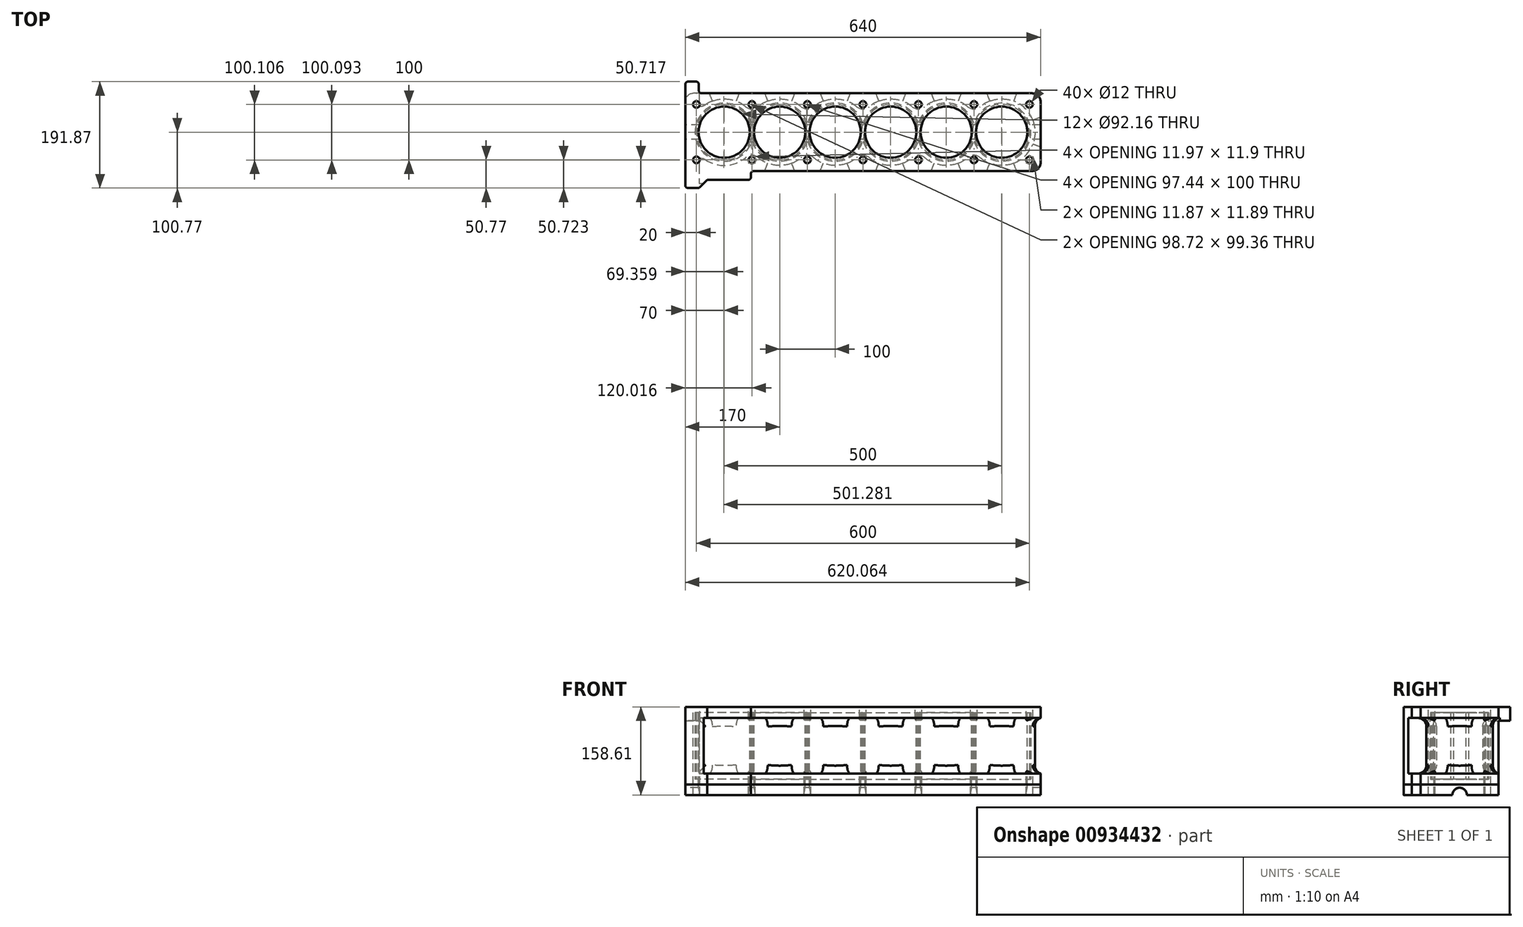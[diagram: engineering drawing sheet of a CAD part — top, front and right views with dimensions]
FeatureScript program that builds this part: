
annotation { "Feature Type Name" : "Feature", "Feature Type Description" : "" }
export const myFeature = defineFeature(function(context is Context, id is Id, definition is map)
    precondition{}
    {
        {
            var Q0;
            Q0=qCreatedBy(makeId("Top.planeOp"),FACE);
            var sketch = newSketch(context, id + "F0", { "sketchPlane" : qUnion([Q0])});
            skCircle(sketch, "E0", {"center": v(0, 0) * mm, "radius": 46.08 * mm});
            skCircle(sketch, "E1.1.0.0", {"center": v(100, 0) * mm, "radius": 46.08 * mm});
            skCircle(sketch, "E1.2.0.0", {"center": v(200, 0) * mm, "radius": 46.08 * mm});
            skCircle(sketch, "E1.3.0.0", {"center": v(300, 0) * mm, "radius": 46.08 * mm});
            skCircle(sketch, "E1.4.0.0", {"center": v(400, 0) * mm, "radius": 46.08 * mm});
            skCircle(sketch, "E1.5.0.0", {"center": v(500, 0) * mm, "radius": 46.08 * mm});
            skLineSegment(sketch, "E1.direction1", {"start": v(46.08, 0) * mm, "end": v(100, 0) * mm, "construction": true});
            skCircle(sketch, "E2", {"center": v(-50, 50) * mm, "radius": 6 * mm});
            skCircle(sketch, "E3.1.0.0", {"center": v(50, 50) * mm, "radius": 6 * mm});
            skCircle(sketch, "E3.2.0.0", {"center": v(150, 50) * mm, "radius": 6 * mm});
            skLineSegment(sketch, "E3.direction1", {"start": v(-50, 50) * mm, "end": v(50, 50) * mm, "construction": true});
            skCircle(sketch, "E4.0.3.0", {"center": v(250, 50) * mm, "radius": 6 * mm});
            skCircle(sketch, "E4.0.4.0", {"center": v(350, 50) * mm, "radius": 6 * mm});
            skCircle(sketch, "E4.0.5.0", {"center": v(450, 50) * mm, "radius": 6 * mm});
            skCircle(sketch, "E4.0.6.0", {"center": v(550, 50) * mm, "radius": 6 * mm});
            skCircle(sketch, "E5.MirrorC", {"center": v(-50, -50) * mm, "radius": 6 * mm});
            skCircle(sketch, "E6.MirrorC", {"center": v(50, -50) * mm, "radius": 6 * mm});
            skCircle(sketch, "E7.MirrorC", {"center": v(150, -50) * mm, "radius": 6 * mm});
            skCircle(sketch, "E8.MirrorC", {"center": v(250, -50) * mm, "radius": 6 * mm});
            skCircle(sketch, "E9.MirrorC", {"center": v(550, -50) * mm, "radius": 6 * mm});
            skCircle(sketch, "E10.MirrorC", {"center": v(450, -50) * mm, "radius": 6 * mm});
            skCircle(sketch, "E11.MirrorC", {"center": v(350, -50) * mm, "radius": 6 * mm});
            skLineSegment(sketch, "E12", {"start": v(-70, 0) * mm, "end": v(-70, 55) * mm});
            skLineSegment(sketch, "E13", {"start": v(53.32, 70) * mm, "end": v(555, 70) * mm});
            skLineSegment(sketch, "E14", {"start": v(570, 55) * mm, "end": v(570, -55) * mm});
            skLineSegment(sketch, "E15", {"start": v(555, -70) * mm, "end": v(-40.56, -70) * mm});
            skLineSegment(sketch, "E16", {"start": v(-70, 0) * mm, "end": v(-70, -55) * mm});
            skPoint(sketch, "E17.visualSharp", {"position": v(-70, 70) * mm});
            skPoint(sketch, "E18.visualSharp", {"position": v(570, 70) * mm});
            skArc(sketch, "E18.filletArc", {"start": v(570, 55) * mm, "mid": v(565.6, 65.6) * mm, "end": v(555, 70) * mm});
            skPoint(sketch, "E19.visualSharp", {"position": v(570, -70) * mm});
            skArc(sketch, "E19.filletArc", {"start": v(555, -70) * mm, "mid": v(565.6, -65.6) * mm, "end": v(570, -55) * mm});
            skPoint(sketch, "E20.visualSharp", {"position": v(-70, -70) * mm});
            skLineSegment(sketch, "E21", {"start": v(-70, 49.2) * mm, "end": v(-70, 55) * mm});
            skLineSegment(sketch, "E22", {"start": v(-65, 100.77) * mm, "end": v(-47.47, 100.77) * mm});
            skLineSegment(sketch, "E23", {"start": v(-43.93, 99.3) * mm, "end": v(-30.74, 86.12) * mm});
            skPoint(sketch, "E24.visualSharp", {"position": v(-70, 100.77) * mm});
            skArc(sketch, "E24.filletArc", {"start": v(-65, 100.77) * mm, "mid": v(-68.54, 99.3) * mm, "end": v(-70, 95.77) * mm});
            skPoint(sketch, "E25.visualSharp", {"position": v(-45.4, 100.77) * mm});
            skArc(sketch, "E25.filletArc", {"start": v(-43.93, 99.3) * mm, "mid": v(-45.55, 100.4) * mm, "end": v(-47.47, 100.77) * mm});
            skPoint(sketch, "E26.visualSharp", {"position": v(-14.62, 70) * mm});
            skLineSegment(sketch, "E27", {"start": v(-45.56, -75) * mm, "end": v(-45.56, -86.1) * mm});
            skLineSegment(sketch, "E28", {"start": v(-70, -55) * mm, "end": v(-70, -55) * mm});
            skLineSegment(sketch, "E29", {"start": v(-50.56, -91.1) * mm, "end": v(-65, -91.1) * mm});
            skPoint(sketch, "E30.visualSharp", {"position": v(-45.56, -70) * mm});
            skArc(sketch, "E30.filletArc", {"start": v(-40.56, -70) * mm, "mid": v(-44.1, -71.46) * mm, "end": v(-45.56, -75) * mm});
            skPoint(sketch, "E31.visualSharp", {"position": v(-70, -91.1) * mm});
            skArc(sketch, "E31.filletArc", {"start": v(-70, -86.1) * mm, "mid": v(-68.54, -89.63) * mm, "end": v(-65, -91.1) * mm});
            skPoint(sketch, "E32.visualSharp", {"position": v(-45.56, -91.1) * mm});
            skArc(sketch, "E32.filletArc", {"start": v(-50.56, -91.1) * mm, "mid": v(-47.03, -89.63) * mm, "end": v(-45.56, -86.1) * mm});
            skLineSegment(sketch, "E33", {"start": v(-40.56, -70) * mm, "end": v(-55, -70) * mm});
            skArc(sketch, "E34.filletArc", {"start": v(-70, -55) * mm, "mid": v(-65.6, -65.6) * mm, "end": v(-55, -70) * mm});
            skLineSegment(sketch, "E35", {"start": v(-70, -55) * mm, "end": v(-70, -86.1) * mm});
            skLineSegment(sketch, "E36", {"start": v(-10.48, 70) * mm, "end": v(-55, 70) * mm});
            skArc(sketch, "E37.filletArc", {"start": v(-55, 70) * mm, "mid": v(-65.6, 65.6) * mm, "end": v(-70, 55) * mm});
            skLineSegment(sketch, "E38", {"start": v(-70, 95.77) * mm, "end": v(-70, 55) * mm});
            skLineSegment(sketch, "E39", {"start": v(-30.74, 86.12) * mm, "end": v(43.32, 86.12) * mm});
            skLineSegment(sketch, "E40", {"start": v(48.32, 81.12) * mm, "end": v(48.32, 75) * mm});
            skPoint(sketch, "E26.filletArc.start.orphan", {"position": v(-17.55, 72.93) * mm});
            skPoint(sketch, "E41.visualSharp", {"position": v(48.32, 86.12) * mm});
            skArc(sketch, "E41.filletArc", {"start": v(48.32, 81.12) * mm, "mid": v(46.86, 84.65) * mm, "end": v(43.32, 86.12) * mm});
            skArc(sketch, "E42.filletArc", {"start": v(48.32, 75) * mm, "mid": v(49.78, 71.46) * mm, "end": v(53.32, 70) * mm});
            skSolve(sketch);
        }
        {
            var Q0;
            Q0=makeQuery(id+"F0.imprint","IMPRINT",FACE,{"disambiguationData":[TD([[makeQuery(id+"F0.imprint","IMPRINT",EDGE,{"derivedFrom":sQuery(id+"F0.wireOp",EDGE,"E0")}),-1.0]])]});
            extrude(context, id + "F1", {"entities" : qUnion([Q0]), "depth" : 140 * mm, "offsetDistance" : 25 * mm});
        }
        {
            var Q0;
            Q0=makeQuery(id+"F0.imprint","IMPRINT",FACE,{"disambiguationData":[TD([[makeQuery(id+"F0.imprint","IMPRINT",EDGE,{"derivedFrom":sQuery(id+"F0.wireOp",EDGE,"E22")}),-1.0]])]});
            var Q1;
            Q1=makeQuery(id+"F0.imprint","IMPRINT",FACE,{"disambiguationData":[TD([[makeQuery(id+"F0.imprint","IMPRINT",EDGE,{"derivedFrom":sQuery(id+"F0.wireOp",EDGE,"E27")}),-1.0]])]});
            extrude(context, id + "F2", {"entities" : qUnion([Q0, Q1]), "operationType" : NewBodyOperationType.ADD, "depth" : 25 * mm, "offsetDistance" : 25 * mm});
        }
        {
            var Q0;
            Q0=makeQuery(id+"F1.opExtrude","CAP_FACE",FACE,{"disambiguationData":[OSD([sQuery(id+"F0.wireOp",EDGE,"E0"),sQuery(id+"F0.wireOp",EDGE,"E1.1.0.0"),sQuery(id+"F0.wireOp",EDGE,"E1.2.0.0"),sQuery(id+"F0.wireOp",EDGE,"E1.3.0.0"),sQuery(id+"F0.wireOp",EDGE,"E1.4.0.0"),sQuery(id+"F0.wireOp",EDGE,"E1.5.0.0"),sQuery(id+"F0.wireOp",EDGE,"E2"),sQuery(id+"F0.wireOp",EDGE,"E3.1.0.0"),sQuery(id+"F0.wireOp",EDGE,"E3.2.0.0"),sQuery(id+"F0.wireOp",EDGE,"E4.0.3.0"),sQuery(id+"F0.wireOp",EDGE,"E4.0.4.0"),sQuery(id+"F0.wireOp",EDGE,"E4.0.5.0"),sQuery(id+"F0.wireOp",EDGE,"E4.0.6.0"),sQuery(id+"F0.wireOp",EDGE,"E5.MirrorC"),sQuery(id+"F0.wireOp",EDGE,"E6.MirrorC"),sQuery(id+"F0.wireOp",EDGE,"E7.MirrorC"),sQuery(id+"F0.wireOp",EDGE,"E8.MirrorC"),sQuery(id+"F0.wireOp",EDGE,"E9.MirrorC"),sQuery(id+"F0.wireOp",EDGE,"E10.MirrorC"),sQuery(id+"F0.wireOp",EDGE,"E11.MirrorC"),sQuery(id+"F0.wireOp",EDGE,"E12"),sQuery(id+"F0.wireOp",EDGE,"E13"),sQuery(id+"F0.wireOp",EDGE,"E14"),sQuery(id+"F0.wireOp",EDGE,"E15"),sQuery(id+"F0.wireOp",EDGE,"E16"),sQuery(id+"F0.wireOp",EDGE,"E18.filletArc"),sQuery(id+"F0.wireOp",EDGE,"E19.filletArc"),sQuery(id+"F0.wireOp",EDGE,"E21"),sQuery(id+"F0.wireOp",EDGE,"E33"),sQuery(id+"F0.wireOp",EDGE,"E34.filletArc"),sQuery(id+"F0.wireOp",EDGE,"E36"),sQuery(id+"F0.wireOp",EDGE,"E37.filletArc")])],"isStart":false});
            cPlane(context, id + "F3", {"entities" : qUnion([Q0]), "cplaneType" : CPlaneType.OFFSET, "offset" : 70 * mm, "oppositeDirection" : true, "width" : 150 * mm, "height" : 150 * mm});
        }
        {
            var Q0;
            Q0=qCreatedBy(id+"F3.planeOp",FACE);
            var sketch = newSketch(context, id + "F4", { "sketchPlane" : qUnion([Q0])});
            skCircle(sketch, "E43", {"center": v(0, 0) * mm, "radius": 46.08 * mm});
            skCircle(sketch, "E44", {"center": v(0, 0) * mm, "radius": 60 * mm});
            skCircle(sketch, "E45.1.0.0", {"center": v(100, 0) * mm, "radius": 60 * mm});
            skCircle(sketch, "E45.2.0.0", {"center": v(200, 0) * mm, "radius": 60 * mm});
            skCircle(sketch, "E45.3.0.0", {"center": v(300, 0) * mm, "radius": 60 * mm});
            skCircle(sketch, "E45.4.0.0", {"center": v(400, 0) * mm, "radius": 60 * mm});
            skCircle(sketch, "E45.5.0.0", {"center": v(500, 0) * mm, "radius": 60 * mm});
            skLineSegment(sketch, "E45.direction1", {"start": v(0, 0) * mm, "end": v(100, 0) * mm, "construction": true});
            skArc(sketch, "E46", {"start": v(61.3, -45.84) * mm, "mid": v(50, -41.71) * mm, "end": v(38.7, -45.84) * mm});
            skArc(sketch, "E47", {"start": v(38.7, -45.84) * mm, "mid": v(50, -76.71) * mm, "end": v(61.3, -45.84) * mm, "construction": true});
            skArc(sketch, "E48", {"start": v(38.7, 45.84) * mm, "mid": v(50, 41.71) * mm, "end": v(61.3, 45.84) * mm});
            skArc(sketch, "E49", {"start": v(61.3, 45.84) * mm, "mid": v(50, 76.71) * mm, "end": v(38.7, 45.84) * mm, "construction": true});
            skArc(sketch, "E50.1.0.0", {"start": v(138.7, 45.84) * mm, "mid": v(150, 41.71) * mm, "end": v(161.3, 45.84) * mm});
            skArc(sketch, "E50.1.0.1", {"start": v(161.3, -45.84) * mm, "mid": v(150, -41.71) * mm, "end": v(138.7, -45.84) * mm});
            skArc(sketch, "E50.2.0.0", {"start": v(238.7, 45.84) * mm, "mid": v(250, 41.71) * mm, "end": v(261.3, 45.84) * mm});
            skArc(sketch, "E50.2.0.1", {"start": v(261.3, -45.84) * mm, "mid": v(250, -41.71) * mm, "end": v(238.7, -45.84) * mm});
            skArc(sketch, "E50.3.0.0", {"start": v(338.7, 45.84) * mm, "mid": v(350, 41.71) * mm, "end": v(361.3, 45.84) * mm});
            skArc(sketch, "E50.3.0.1", {"start": v(361.3, -45.84) * mm, "mid": v(350, -41.71) * mm, "end": v(338.7, -45.84) * mm});
            skArc(sketch, "E50.4.0.0", {"start": v(438.7, 45.84) * mm, "mid": v(450, 41.71) * mm, "end": v(461.3, 45.84) * mm});
            skArc(sketch, "E50.4.0.1", {"start": v(461.3, -45.84) * mm, "mid": v(450, -41.71) * mm, "end": v(438.7, -45.84) * mm});
            skLineSegment(sketch, "E50.direction1", {"start": v(38.7, 45.84) * mm, "end": v(138.7, 45.84) * mm, "construction": true});
            skLineSegment(sketch, "E51", {"start": v(0, 92.54) * mm, "end": v(500, 92.54) * mm});
            skLineSegment(sketch, "E52", {"start": v(500, 92.54) * mm, "end": v(500, 0) * mm});
            skLineSegment(sketch, "E53.MirrorCS", {"start": v(0, -92.54) * mm, "end": v(500, -92.54) * mm});
            skLineSegment(sketch, "E54.MirrorCS", {"start": v(500, -92.54) * mm, "end": v(500, 0) * mm});
            skLineSegment(sketch, "E55", {"start": v(500, 92.54) * mm, "end": v(617.88, 92.54) * mm});
            skLineSegment(sketch, "E56", {"start": v(617.88, 92.54) * mm, "end": v(617.88, -92.54) * mm});
            skLineSegment(sketch, "E57", {"start": v(617.88, -92.54) * mm, "end": v(500, -92.54) * mm});
            skLineSegment(sketch, "E58", {"start": v(0, -92.54) * mm, "end": v(-115.44, -92.54) * mm});
            skLineSegment(sketch, "E59", {"start": v(-115.44, -92.54) * mm, "end": v(-115.44, 92.54) * mm});
            skLineSegment(sketch, "E60", {"start": v(-115.44, 92.54) * mm, "end": v(0, 92.54) * mm});
            skLineSegment(sketch, "E61", {"start": v(-44.8, -92.54) * mm, "end": v(-44.8, 92.54) * mm});
            skPoint(sketch, "E62.MirrorCS.end.orphan", {"position": v(0, -92.54) * mm});
            skPoint(sketch, "E62.MirrorCS.start.orphan", {"position": v(0, -60) * mm});
            skPoint(sketch, "E63.start.orphan", {"position": v(0, 60) * mm});
            skSolve(sketch);
        }
        {
            var Q0;
            {var subQ5=sQuery(id+"F4.wireOp",EDGE,"E48");Q0=makeQuery(id+"F4.imprint","IMPRINT",FACE,{"disambiguationData":[TD([[makeQuery(id+"F4.imprint","IMPRINT",EDGE,{"derivedFrom":subQ5}),1.0]])]});}
            var Q1;
            {var subQ2=sQuery(id+"F4.wireOp",EDGE,"E46");Q1=makeQuery(id+"F4.imprint","IMPRINT",FACE,{"disambiguationData":[TD([[makeQuery(id+"F4.imprint","IMPRINT",EDGE,{"derivedFrom":subQ2}),1.0]])]});}
            var Q2;
            {var subQ0=sQuery(id+"F4.wireOp",EDGE,"E55");Q2=makeQuery(id+"F4.imprint","IMPRINT",FACE,{"disambiguationData":[TD([[makeQuery(id+"F4.imprint","IMPRINT",EDGE,{"derivedFrom":subQ0}),-1.0]])]});}
            extrude(context, id + "F5", {"entities" : qUnion([Q0, Q1, Q2]), "operationType" : NewBodyOperationType.REMOVE, "endBound" : BoundingType.SYMMETRIC, "oppositeDirection" : true, "depth" : 100 * mm, "offsetDistance" : 25 * mm});
        }
        {
            var Q0;
            {var subQ0=sQuery(id+"F4.wireOp",EDGE,"E45.4.0.0");Q0=makeQuery(id+"F5.boolean.opBoolean","COPY",EDGE,{"derivedFrom":makeQuery(id+"F5.opExtrude","CAP_EDGE",EDGE,{"disambiguationData":[OSD([subQ0]),TDD([makeQuery(id+"F4.imprint","IMPRINT",EDGE,{"disambiguationData":[TD([[makeQuery(id+"F4.imprint","INTERSECT",VERTEX,{"derivedFrom":[subQ0,sQuery(id+"F4.wireOp",EDGE,"E50.3.0.0")]}),1.0]])],"derivedFrom":subQ0})])],"isStart":true})});}
            var Q1;
            {var subQ0=sQuery(id+"F4.wireOp",EDGE,"E45.3.0.0");Q1=makeQuery(id+"F5.boolean.opBoolean","COPY",EDGE,{"derivedFrom":makeQuery(id+"F5.opExtrude","CAP_EDGE",EDGE,{"disambiguationData":[OSD([subQ0]),TDD([makeQuery(id+"F4.imprint","IMPRINT",EDGE,{"disambiguationData":[TD([[makeQuery(id+"F4.imprint","INTERSECT",VERTEX,{"derivedFrom":[subQ0,sQuery(id+"F4.wireOp",EDGE,"E50.2.0.0")]}),1.0]])],"derivedFrom":subQ0})])],"isStart":false})});}
            fillet(context, id + "F6", {"entities" : qUnion([Q0, Q1]), "radius" : 15 * mm, "tangentPropagation" : true, "allowEdgeOverflow" : false});
        }
        {
            var Q0;
            Q0=makeQuery(id+"F5.boolean.opBoolean","COPY",EDGE,{"derivedFrom":makeQuery(id+"F5.opExtrude","SWEPT_EDGE",EDGE,{"disambiguationData":[OSD([sQuery(id+"F4.wireOp",EDGE,"E44"),sQuery(id+"F4.wireOp",EDGE,"E62.MirrorCS")])]})});
            var Q1;
            Q1=makeQuery(id+"F5.boolean.opBoolean","COPY",EDGE,{"derivedFrom":makeQuery(id+"F5.opExtrude","SWEPT_EDGE",EDGE,{"disambiguationData":[OSD([sQuery(id+"F4.wireOp",EDGE,"E44"),sQuery(id+"F4.wireOp",EDGE,"E63")])]})});
            fillet(context, id + "F7", {"entities" : qUnion([Q0, Q1]), "radius" : 15 * mm, "tangentPropagation" : true, "allowEdgeOverflow" : false});
        }
        {
            var Q0;
            Q0=qCreatedBy(id+"F3.planeOp",FACE);
            var sketch = newSketch(context, id + "F8", { "sketchPlane" : qUnion([Q0])});
            skArc(sketch, "E64", {"start": v(48.72, 11.25) * mm, "mid": v(-50, 0) * mm, "end": v(48.72, -11.25) * mm});
            skArc(sketch, "E65", {"start": v(50, 16) * mm, "mid": v(-52.5, 0) * mm, "end": v(50, -16) * mm});
            skArc(sketch, "E66.1.0.0", {"start": v(48.72, 11.25) * mm, "mid": v(47.5, 0) * mm, "end": v(48.72, -11.25) * mm});
            skArc(sketch, "E66.1.0.1", {"start": v(51.28, -11.25) * mm, "mid": v(100, -50) * mm, "end": v(148.72, -11.25) * mm});
            skArc(sketch, "E66.2.0.0", {"start": v(148.72, 11.25) * mm, "mid": v(147.5, 0) * mm, "end": v(148.72, -11.25) * mm});
            skArc(sketch, "E66.2.0.1", {"start": v(151.28, -11.25) * mm, "mid": v(200, -50) * mm, "end": v(248.72, -11.25) * mm});
            skArc(sketch, "E66.3.0.0", {"start": v(248.72, 11.25) * mm, "mid": v(247.5, 0) * mm, "end": v(248.72, -11.25) * mm});
            skArc(sketch, "E66.3.0.1", {"start": v(251.28, -11.25) * mm, "mid": v(300, -50) * mm, "end": v(348.72, -11.25) * mm});
            skArc(sketch, "E66.4.0.0", {"start": v(348.72, 11.25) * mm, "mid": v(347.5, 0) * mm, "end": v(348.72, -11.25) * mm});
            skArc(sketch, "E66.4.0.1", {"start": v(351.28, -11.25) * mm, "mid": v(400, -50) * mm, "end": v(448.72, -11.25) * mm});
            skArc(sketch, "E66.5.0.0", {"start": v(448.72, 11.25) * mm, "mid": v(447.5, 0) * mm, "end": v(448.72, -11.25) * mm});
            skArc(sketch, "E66.5.0.1", {"start": v(451.28, -11.25) * mm, "mid": v(550, 0) * mm, "end": v(451.28, 11.25) * mm});
            skLineSegment(sketch, "E66.direction1", {"start": v(0, 0) * mm, "end": v(100, 0) * mm, "construction": true});
            skArc(sketch, "E67.trimOffspring", {"start": v(51.28, -11.25) * mm, "mid": v(52.5, 0) * mm, "end": v(51.28, 11.25) * mm});
            skArc(sketch, "E68.trimOffspring", {"start": v(50, -16) * mm, "mid": v(100, -52.5) * mm, "end": v(150, -16) * mm});
            skArc(sketch, "E69.trimOffspring", {"start": v(148.72, 11.25) * mm, "mid": v(100, 50) * mm, "end": v(51.28, 11.25) * mm});
            skArc(sketch, "E70.trimOffspring", {"start": v(150, 16) * mm, "mid": v(100, 52.5) * mm, "end": v(50, 16) * mm});
            skArc(sketch, "E71.trimOffspring", {"start": v(150, -16) * mm, "mid": v(200, -52.5) * mm, "end": v(250, -16) * mm});
            skArc(sketch, "E72.trimOffspring", {"start": v(151.28, -11.25) * mm, "mid": v(152.5, 0) * mm, "end": v(151.28, 11.25) * mm});
            skArc(sketch, "E73.trimOffspring", {"start": v(248.72, 11.25) * mm, "mid": v(200, 50) * mm, "end": v(151.28, 11.25) * mm});
            skArc(sketch, "E74.trimOffspring", {"start": v(250, 16) * mm, "mid": v(200, 52.5) * mm, "end": v(150, 16) * mm});
            skArc(sketch, "E75.trimOffspring", {"start": v(251.28, -11.25) * mm, "mid": v(252.5, 0) * mm, "end": v(251.28, 11.25) * mm});
            skArc(sketch, "E76.trimOffspring", {"start": v(250, -16) * mm, "mid": v(300, -52.5) * mm, "end": v(350, -16) * mm});
            skArc(sketch, "E77.trimOffspring", {"start": v(350, 16) * mm, "mid": v(300, 52.5) * mm, "end": v(250, 16) * mm});
            skArc(sketch, "E78.trimOffspring", {"start": v(348.72, 11.25) * mm, "mid": v(300, 50) * mm, "end": v(251.28, 11.25) * mm});
            skArc(sketch, "E79.trimOffspring", {"start": v(351.28, -11.25) * mm, "mid": v(352.5, 0) * mm, "end": v(351.28, 11.25) * mm});
            skArc(sketch, "E80.trimOffspring", {"start": v(350, -16) * mm, "mid": v(400, -52.5) * mm, "end": v(450, -16) * mm});
            skArc(sketch, "E81.trimOffspring", {"start": v(448.72, 11.25) * mm, "mid": v(400, 50) * mm, "end": v(351.28, 11.25) * mm});
            skArc(sketch, "E82.trimOffspring", {"start": v(450, 16) * mm, "mid": v(400, 52.5) * mm, "end": v(350, 16) * mm});
            skArc(sketch, "E83.trimOffspring", {"start": v(451.28, -11.25) * mm, "mid": v(452.5, 0) * mm, "end": v(451.28, 11.25) * mm});
            skArc(sketch, "E84.trimOffspring", {"start": v(450, -16) * mm, "mid": v(552.5, 0) * mm, "end": v(450, 16) * mm});
            skSolve(sketch);
        }
        {
            var Q0;
            Q0=makeQuery(id+"F8.imprint","IMPRINT",FACE,{"disambiguationData":[TD([[makeQuery(id+"F8.imprint","IMPRINT",EDGE,{"derivedFrom":sQuery(id+"F8.wireOp",EDGE,"E64")}),-1.0]])]});
            extrude(context, id + "F9", {"entities" : qUnion([Q0]), "operationType" : NewBodyOperationType.REMOVE, "endBound" : BoundingType.SYMMETRIC, "oppositeDirection" : true, "depth" : 120 * mm, "offsetDistance" : 25 * mm});
        }
        {
            var Q0;
            Q0=makeQuery(id+"F1.opExtrude","SWEPT_BODY",BODY,{"disambiguationData":[OSD([sQuery(id+"F0.wireOp",EDGE,"E0"),sQuery(id+"F0.wireOp",EDGE,"E1.1.0.0"),sQuery(id+"F0.wireOp",EDGE,"E1.2.0.0"),sQuery(id+"F0.wireOp",EDGE,"E1.3.0.0"),sQuery(id+"F0.wireOp",EDGE,"E1.4.0.0"),sQuery(id+"F0.wireOp",EDGE,"E1.5.0.0"),sQuery(id+"F0.wireOp",EDGE,"E2"),sQuery(id+"F0.wireOp",EDGE,"E3.1.0.0"),sQuery(id+"F0.wireOp",EDGE,"E3.2.0.0"),sQuery(id+"F0.wireOp",EDGE,"E4.0.3.0"),sQuery(id+"F0.wireOp",EDGE,"E4.0.4.0"),sQuery(id+"F0.wireOp",EDGE,"E4.0.5.0"),sQuery(id+"F0.wireOp",EDGE,"E4.0.6.0"),sQuery(id+"F0.wireOp",EDGE,"E5.MirrorC"),sQuery(id+"F0.wireOp",EDGE,"E6.MirrorC"),sQuery(id+"F0.wireOp",EDGE,"E7.MirrorC"),sQuery(id+"F0.wireOp",EDGE,"E8.MirrorC"),sQuery(id+"F0.wireOp",EDGE,"E9.MirrorC"),sQuery(id+"F0.wireOp",EDGE,"E10.MirrorC"),sQuery(id+"F0.wireOp",EDGE,"E11.MirrorC"),sQuery(id+"F0.wireOp",EDGE,"E12"),sQuery(id+"F0.wireOp",EDGE,"E13"),sQuery(id+"F0.wireOp",EDGE,"E14"),sQuery(id+"F0.wireOp",EDGE,"E15"),sQuery(id+"F0.wireOp",EDGE,"E16"),sQuery(id+"F0.wireOp",EDGE,"E18.filletArc"),sQuery(id+"F0.wireOp",EDGE,"E19.filletArc"),sQuery(id+"F0.wireOp",EDGE,"E21"),sQuery(id+"F0.wireOp",EDGE,"E33"),sQuery(id+"F0.wireOp",EDGE,"E34.filletArc"),sQuery(id+"F0.wireOp",EDGE,"E36"),sQuery(id+"F0.wireOp",EDGE,"E37.filletArc")])]});
            var Q1;
            Q1=sQuery(id+"F8.wireOp",EDGE,"E66.direction1");
            transform(context, id + "F10", {"entities" : qUnion([Q0]), "transformType" : TransformType.ROTATION, "transformAxis" : qUnion([Q1]), "angle" : 180 * degree, "makeCopy" : false});
        }
        {
            var Q0;
            Q0=makeQuery(id+"F1.opExtrude","CAP_FACE",FACE,{"disambiguationData":[OSD([sQuery(id+"F0.wireOp",EDGE,"E0"),sQuery(id+"F0.wireOp",EDGE,"E1.1.0.0"),sQuery(id+"F0.wireOp",EDGE,"E1.2.0.0"),sQuery(id+"F0.wireOp",EDGE,"E1.3.0.0"),sQuery(id+"F0.wireOp",EDGE,"E1.4.0.0"),sQuery(id+"F0.wireOp",EDGE,"E1.5.0.0"),sQuery(id+"F0.wireOp",EDGE,"E2"),sQuery(id+"F0.wireOp",EDGE,"E3.1.0.0"),sQuery(id+"F0.wireOp",EDGE,"E3.2.0.0"),sQuery(id+"F0.wireOp",EDGE,"E4.0.3.0"),sQuery(id+"F0.wireOp",EDGE,"E4.0.4.0"),sQuery(id+"F0.wireOp",EDGE,"E4.0.5.0"),sQuery(id+"F0.wireOp",EDGE,"E4.0.6.0"),sQuery(id+"F0.wireOp",EDGE,"E5.MirrorC"),sQuery(id+"F0.wireOp",EDGE,"E6.MirrorC"),sQuery(id+"F0.wireOp",EDGE,"E7.MirrorC"),sQuery(id+"F0.wireOp",EDGE,"E8.MirrorC"),sQuery(id+"F0.wireOp",EDGE,"E9.MirrorC"),sQuery(id+"F0.wireOp",EDGE,"E10.MirrorC"),sQuery(id+"F0.wireOp",EDGE,"E11.MirrorC"),sQuery(id+"F0.wireOp",EDGE,"E12"),sQuery(id+"F0.wireOp",EDGE,"E13"),sQuery(id+"F0.wireOp",EDGE,"E14"),sQuery(id+"F0.wireOp",EDGE,"E15"),sQuery(id+"F0.wireOp",EDGE,"E16"),sQuery(id+"F0.wireOp",EDGE,"E18.filletArc"),sQuery(id+"F0.wireOp",EDGE,"E19.filletArc"),sQuery(id+"F0.wireOp",EDGE,"E21"),sQuery(id+"F0.wireOp",EDGE,"E22"),sQuery(id+"F0.wireOp",EDGE,"E23"),sQuery(id+"F0.wireOp",EDGE,"E24.filletArc"),sQuery(id+"F0.wireOp",EDGE,"E25.filletArc"),sQuery(id+"F0.wireOp",EDGE,"E33"),sQuery(id+"F0.wireOp",EDGE,"E34.filletArc"),sQuery(id+"F0.wireOp",EDGE,"E38"),sQuery(id+"F0.wireOp",EDGE,"E39"),sQuery(id+"F0.wireOp",EDGE,"E40"),sQuery(id+"F0.wireOp",EDGE,"E41.filletArc"),sQuery(id+"F0.wireOp",EDGE,"E42.filletArc")])],"isStart":false});
            extrude(context, id + "F11", {"entities" : qUnion([Q0]), "depth" : 18.6 * mm, "offsetDistance" : 25 * mm});
        }
        {
            var Q0;
            {var subQ0=sQuery(id+"F0.wireOp",EDGE,"E38");var subQ1=sQuery(id+"F0.wireOp",EDGE,"E21");var subQ2=sQuery(id+"F0.wireOp",EDGE,"E16");var subQ3=sQuery(id+"F0.wireOp",EDGE,"E12");Q0=makeQuery(id+"F11.boolean.opBoolean","MERGE",FACE,{"derivedFrom":[makeQuery(id+"F2.boolean.opBoolean","MERGE",FACE,{"derivedFrom":[makeQuery(id+"F1.opExtrude","SWEPT_FACE",FACE,{"disambiguationData":[OSD([subQ3,subQ2,subQ1,subQ0])]}),makeQuery(id+"F2.opExtrude","SWEPT_FACE",FACE,{"disambiguationData":[OSD([subQ3,subQ2,subQ1,sQuery(id+"F0.wireOp",EDGE,"E35"),subQ0])]})]}),makeQuery(id+"F11.opExtrude","SWEPT_FACE",FACE,{"disambiguationData":[OSD([subQ3,subQ2,subQ1,subQ0])]})]});}
            var sketch = newSketch(context, id + "F12", { "sketchPlane" : qUnion([Q0])});
            skCircle(sketch, "E85", {"center": v(0, -18.6) * mm, "radius": 13 * mm});
            skSolve(sketch);
        }
        {
            var Q0;
            Q0 = qSketchRegion(id + "F12", true);
            extrude(context, id + "F13", {"entities" : qUnion([Q0]), "operationType" : NewBodyOperationType.REMOVE, "endBound" : BoundingType.THROUGH_ALL, "oppositeDirection" : true, "depth" : 25 * mm, "offsetDistance" : 25 * mm});
        }
    });
